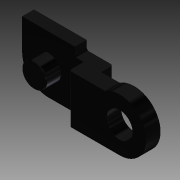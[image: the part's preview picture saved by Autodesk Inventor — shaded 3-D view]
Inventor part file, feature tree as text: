
AUTODESK INVENTOR PART (.ipt)
format: ipt  version: 2013 (Build 170138000, 138)  size: 106,496 bytes
history: native  units: in
note: dims shown in document units (in); Inventor stores cm internally (conversion verified against a paired STEP export)
features: other x1, imported_body x1, extrude x1, sketch x1
ambient origin geometry x8: Origin, YZ Plane, XZ Plane, XY Plane, X Axis, Y Axis, Z Axis, Center Point
feature tree (4):
  other  "TETRIX_TT_LINK_2_2011"
  imported_body  "Base1"
  extrude  "Extrusion1"  [1 undecoded]
  sketch  "Sketch2"  dims[d0=0.006in d1=0.0in]
note: 1 required parameter value undecoded (feature->parameter linkage not recoverable at this tier; creation-order binding heuristic only, values carry confidence <= 0.55)
